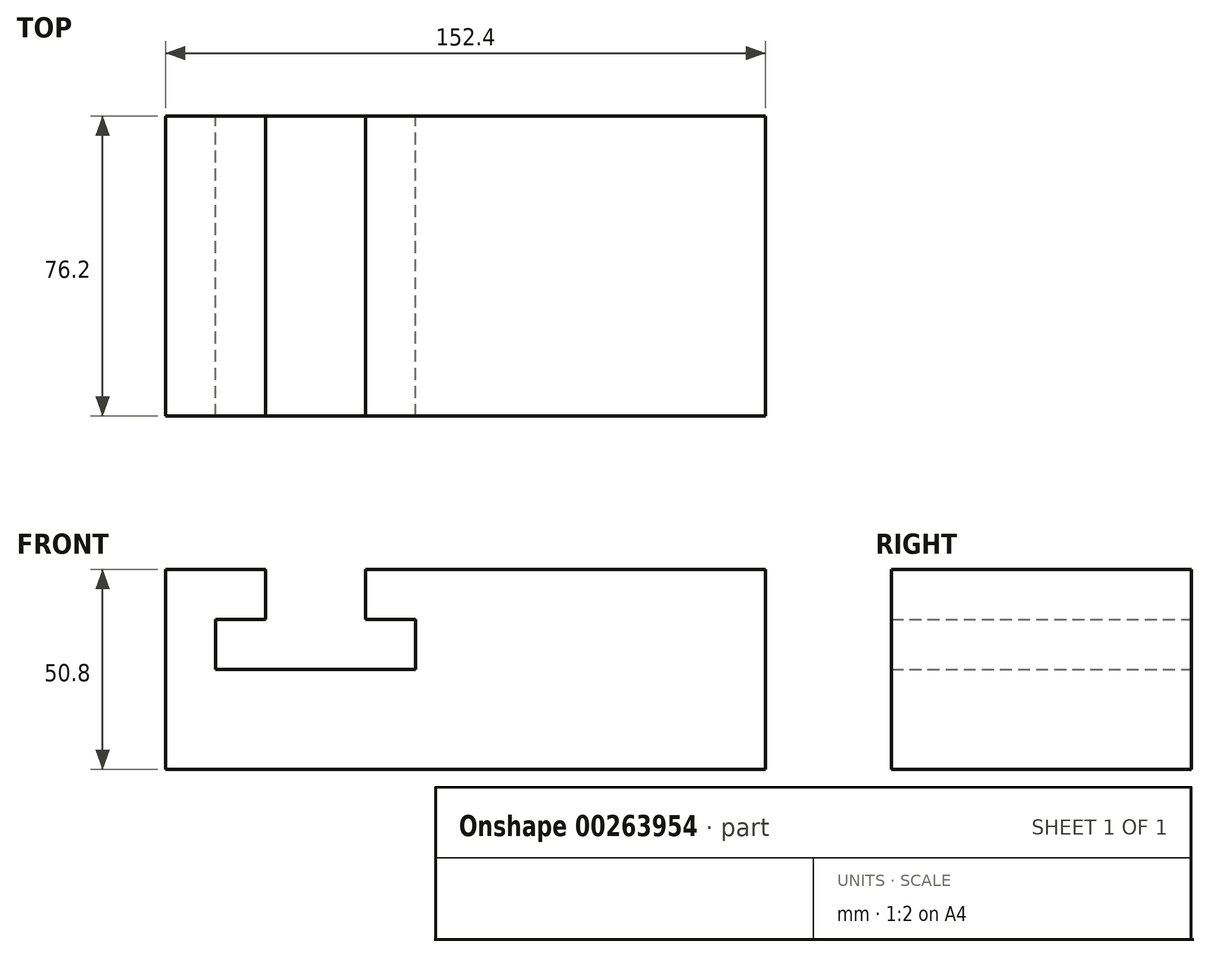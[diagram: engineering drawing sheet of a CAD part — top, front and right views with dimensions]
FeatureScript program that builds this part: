
annotation { "Feature Type Name" : "Feature", "Feature Type Description" : "" }
export const myFeature = defineFeature(function(context is Context, id is Id, definition is map)
    precondition{}
    {
        {
            var Q0;
            Q0=qCreatedBy(makeId("Front.planeOp"),FACE);
            var sketch = newSketch(context, id + "F0", { "sketchPlane" : qUnion([Q0])});
            skLineSegment(sketch, "E0.bottom", {"start": v(-120.2, 0) * mm, "end": v(32.2, 0) * mm});
            skLineSegment(sketch, "E0.top", {"start": v(-120.2, -50.8) * mm, "end": v(32.2, -50.8) * mm});
            skLineSegment(sketch, "E0.left", {"start": v(-120.2, 0) * mm, "end": v(-120.2, -50.8) * mm});
            skLineSegment(sketch, "E0.right", {"start": v(32.2, 0) * mm, "end": v(32.2, -50.8) * mm});
            skLineSegment(sketch, "E1", {"start": v(-120.2, 0) * mm, "end": v(-94.8, 0) * mm});
            skLineSegment(sketch, "E2", {"start": v(-94.8, 0) * mm, "end": v(-69.4, 0) * mm});
            skLineSegment(sketch, "E3", {"start": v(-69.4, 0) * mm, "end": v(-44, 0) * mm});
            skLineSegment(sketch, "E4", {"start": v(-94.8, 0) * mm, "end": v(-94.8, -12.7) * mm});
            skLineSegment(sketch, "E5", {"start": v(-94.8, -12.7) * mm, "end": v(-107.5, -12.7) * mm});
            skLineSegment(sketch, "E6", {"start": v(-69.4, 0) * mm, "end": v(-69.4, -12.7) * mm});
            skLineSegment(sketch, "E7", {"start": v(-69.4, -12.7) * mm, "end": v(-56.7, -12.7) * mm});
            skLineSegment(sketch, "E8", {"start": v(-107.5, -12.7) * mm, "end": v(-107.5, -25.4) * mm});
            skLineSegment(sketch, "E9", {"start": v(-56.7, -12.7) * mm, "end": v(-56.7, -25.4) * mm});
            skLineSegment(sketch, "E10", {"start": v(-107.5, -25.4) * mm, "end": v(-56.7, -25.4) * mm});
            skSolve(sketch);
        }
        {
            var Q0;
            Q0=makeQuery(id+"F0.imprint","IMPRINT",FACE,{"disambiguationData":[TD([[makeQuery(id+"F0.imprint","IMPRINT",EDGE,{"derivedFrom":sQuery(id+"F0.wireOp",EDGE,"E0.bottom")}),-1.0]])]});
            var Q1;
            Q1=makeQuery(id+"F0.imprint","IMPRINT",FACE,{"disambiguationData":[TD([[makeQuery(id+"F0.imprint","IMPRINT",EDGE,{"derivedFrom":sQuery(id+"F0.wireOp",EDGE,"E0.bottom")}),-1.0]])]});
            extrude(context, id + "F1", {"entities" : qUnion([Q0, Q1]), "depth" : 76.2 * mm});
        }
    });
